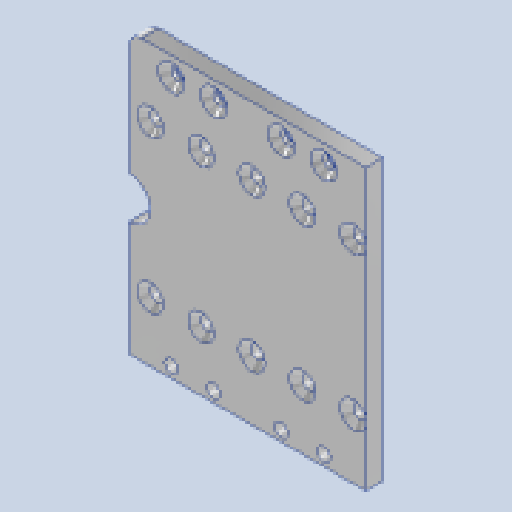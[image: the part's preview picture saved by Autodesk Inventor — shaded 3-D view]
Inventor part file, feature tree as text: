
AUTODESK INVENTOR PART (.ipt)
format: ipt  version: 2023.1 (Build 271208000, 208)  size: 264,192 bytes
history: native  units: mm
features: extrude x5, sketch x5, projected_geometry x3, chamfer x2, other x1, fillet x1
ambient origin geometry x8: Origin, YZ Plane, XZ Plane, XY Plane, X Axis, Y Axis, Z Axis, Center Point
bodies: Body1 (feature_tree)
feature tree (17):
  other  "솔리드1"
  extrude  "돌출1"  Depth=66.2mm
  extrude  "돌출2"  Depth=5.1mm
  extrude  "돌출3"  Depth=4.0mm TaperAngle=0.0deg
  extrude  "돌출4"  Depth=2.0mm
  extrude  "돌출5"  Depth=28.0mm
  fillet  "모깎기1"  Radius=28.0mm
  chamfer  "모따기1"  Distance=4.0mm
  chamfer  "모따기2"  Distance=18.0mm
  sketch  "스케치1"
  sketch  "스케치2"
  sketch  "스케치3"
  projected_geometry  "투영된 루프1"
  sketch  "스케치4"
  projected_geometry  "투영된 루프2"
  sketch  "스케치5"
  projected_geometry  "투영된 루프3"
